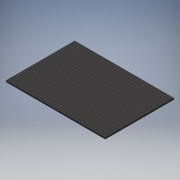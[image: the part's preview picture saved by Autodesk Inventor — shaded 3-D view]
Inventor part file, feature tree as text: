
AUTODESK INVENTOR PART (.ipt)
format: ipt  version: 2017 (Build 210142000, 142)  size: 100,864 bytes
history: native  units: mm
features: extrude x1, sketch x1
ambient origin geometry x8: Origin, YZ Plane, XZ Plane, XY Plane, X Axis, Y Axis, Z Axis, Center Point
bodies: Volumenkörper1 (feature_tree)
feature tree (2):
  extrude  "Extrusion1"  Depth=6500.0mm
  sketch  "Skizze1"  dims[d0=4500.0mm d1=6500.0mm d2=100.0mm d3=0.0mm]
